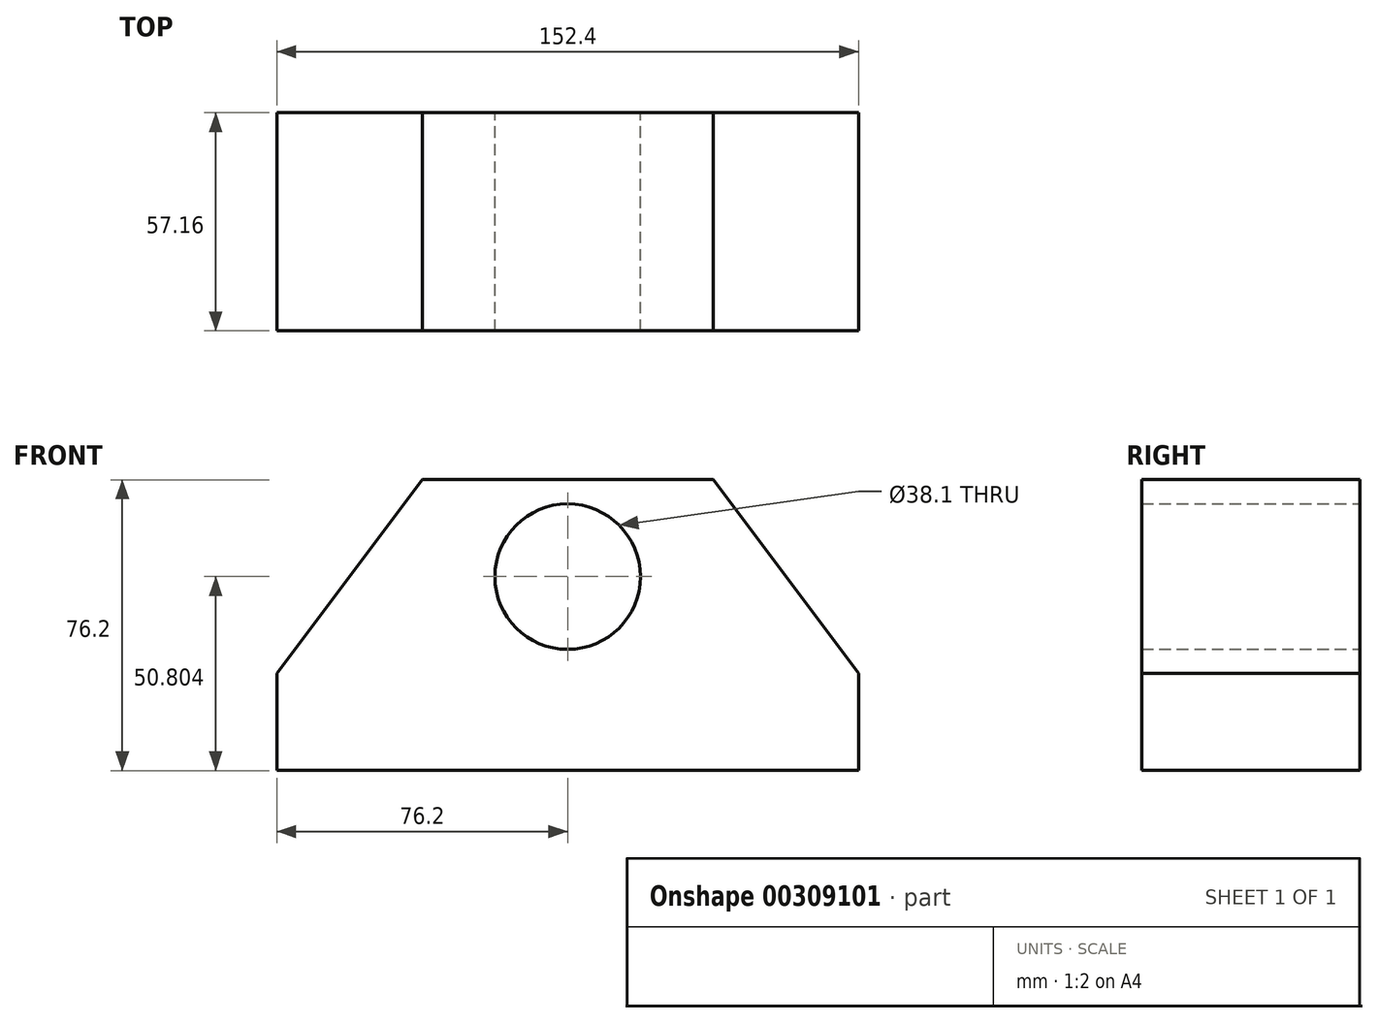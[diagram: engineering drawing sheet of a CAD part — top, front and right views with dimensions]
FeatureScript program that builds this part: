
annotation { "Feature Type Name" : "Feature", "Feature Type Description" : "" }
export const myFeature = defineFeature(function(context is Context, id is Id, definition is map)
    precondition{}
    {
        {
            var Q0;
            Q0=qCreatedBy(makeId("Front.planeOp"),FACE);
            var sketch = newSketch(context, id + "F0", { "sketchPlane" : qUnion([Q0])});
            skLineSegment(sketch, "E0.bottom", {"start": v(-76.2, -30.53) * mm, "end": v(76.2, -30.53) * mm});
            skLineSegment(sketch, "E0.left", {"start": v(-76.2, -30.53) * mm, "end": v(-76.2, -5.13) * mm});
            skLineSegment(sketch, "E0.right", {"start": v(76.2, -30.53) * mm, "end": v(76.2, -5.13) * mm});
            skLineSegment(sketch, "E1", {"start": v(-76.2, -5.13) * mm, "end": v(-38.1, 45.67) * mm});
            skLineSegment(sketch, "E2", {"start": v(76.2, -5.13) * mm, "end": v(38.1, 45.67) * mm});
            skLineSegment(sketch, "E3", {"start": v(-38.1, 45.67) * mm, "end": v(38.1, 45.67) * mm});
            skCircle(sketch, "E4", {"center": v(0, 20.27) * mm, "radius": 19.05 * mm});
            skSolve(sketch);
        }
        {
            var Q0;
            Q0=makeQuery(id+"F0.imprint","IMPRINT",FACE,{"disambiguationData":[TD([[makeQuery(id+"F0.imprint","IMPRINT",EDGE,{"derivedFrom":sQuery(id+"F0.wireOp",EDGE,"E0.bottom")}),1.0]])]});
            extrude(context, id + "F1", {"entities" : qUnion([Q0]), "depth" : 57.15 * mm, "symmetric" : true});
        }
    });
